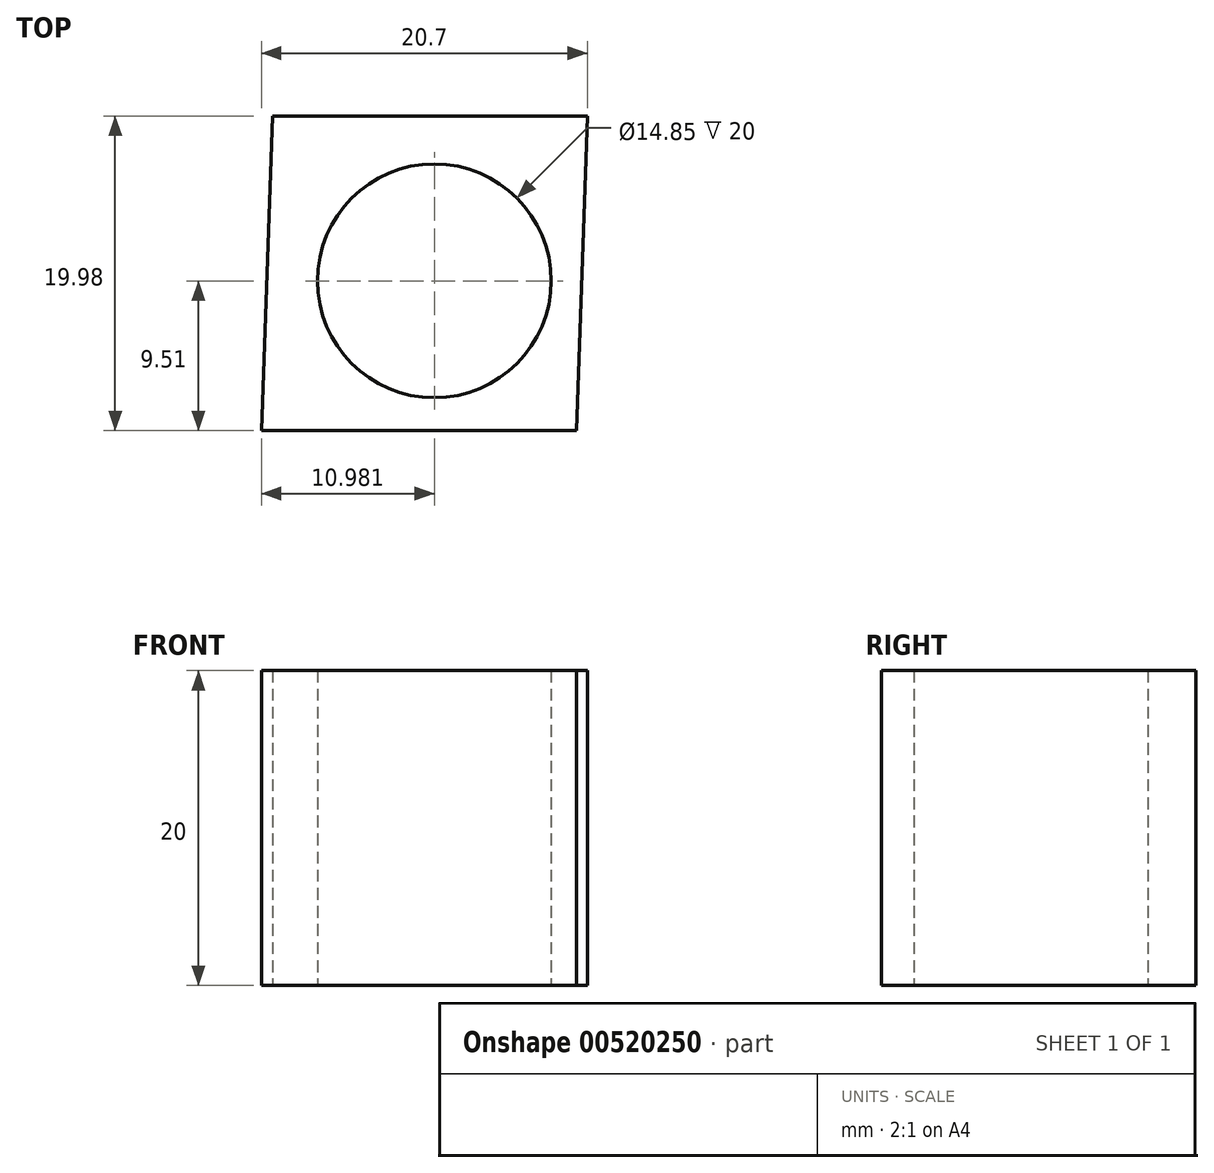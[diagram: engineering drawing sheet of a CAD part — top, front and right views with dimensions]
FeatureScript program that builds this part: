
annotation { "Feature Type Name" : "Feature", "Feature Type Description" : "" }
export const myFeature = defineFeature(function(context is Context, id is Id, definition is map)
    precondition{}
    {
        {
            var Q0;
            Q0=qCreatedBy(makeId("Top.planeOp"),FACE);
            var sketch = newSketch(context, id + "F0", { "sketchPlane" : qUnion([Q0])});
            skLineSegment(sketch, "E0", {"start": v(11.9, -9.51) * mm, "end": v(12.6, 10.47) * mm});
            skLineSegment(sketch, "E1", {"start": v(12.6, 10.47) * mm, "end": v(32.6, 10.47) * mm});
            skLineSegment(sketch, "E2", {"start": v(32.6, 10.47) * mm, "end": v(31.9, -9.51) * mm});
            skLineSegment(sketch, "E3", {"start": v(31.9, -9.51) * mm, "end": v(11.9, -9.51) * mm});
            skCircle(sketch, "E4", {"center": v(22.88, 0) * mm, "radius": 7.42 * mm});
            skSolve(sketch);
        }
        {
            var Q0;
            Q0=makeQuery(id+"F0.imprint","IMPRINT",FACE,{"disambiguationData":[TD([[makeQuery(id+"F0.imprint","IMPRINT",EDGE,{"derivedFrom":sQuery(id+"F0.wireOp",EDGE,"E0")}),-1.0]])]});
            extrude(context, id + "F1", {"entities" : qUnion([Q0]), "depth" : 20 * mm, "offsetDistance" : 25 * mm});
        }
    });
